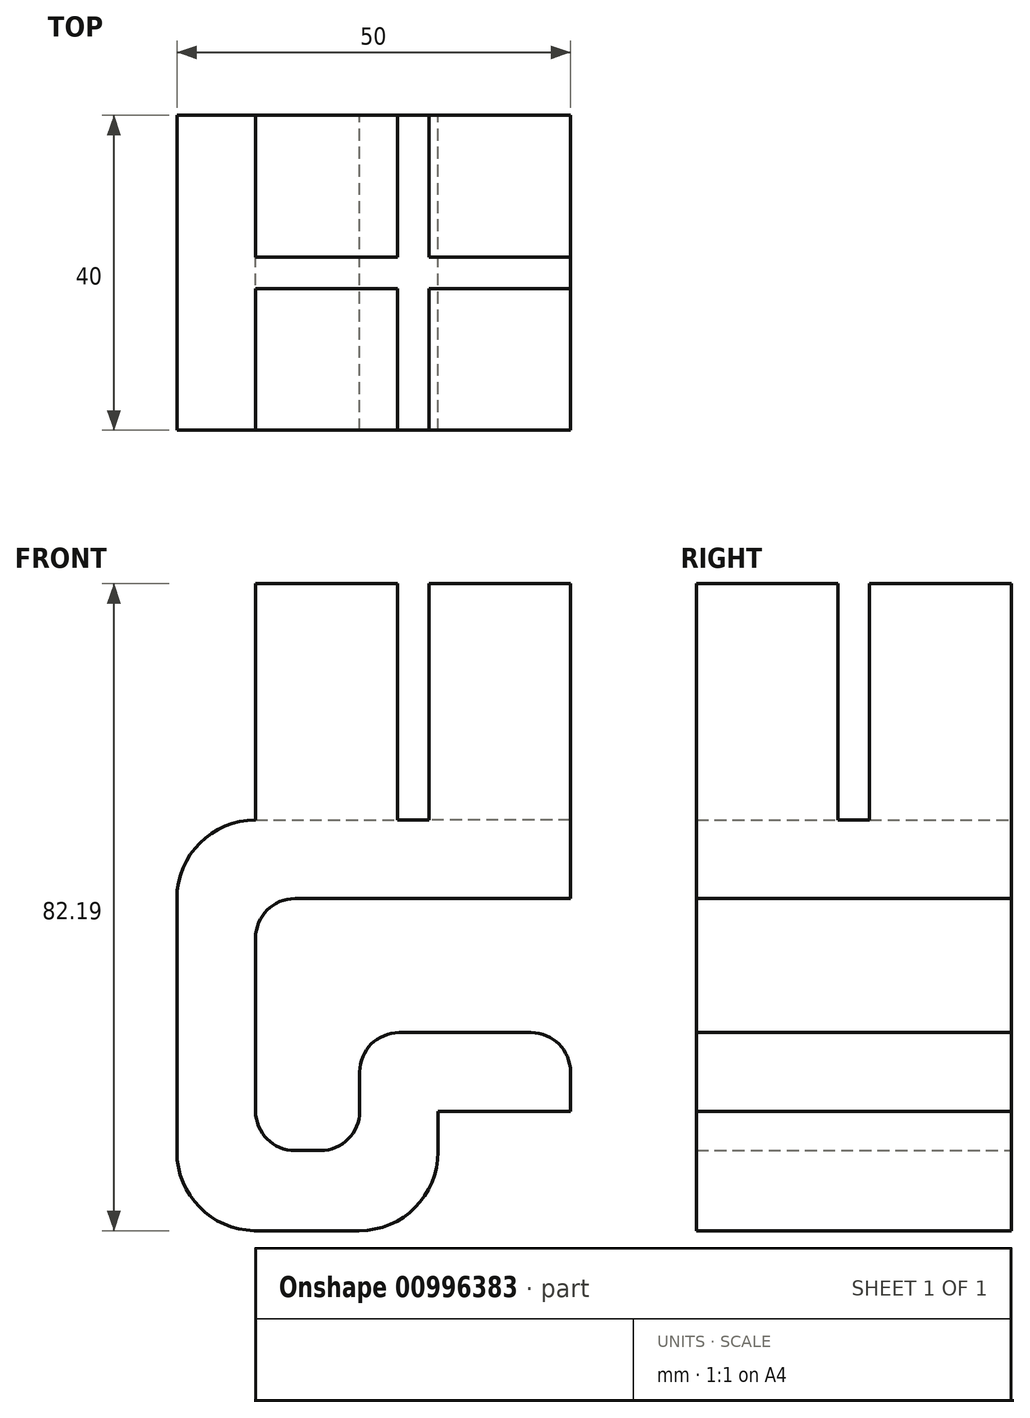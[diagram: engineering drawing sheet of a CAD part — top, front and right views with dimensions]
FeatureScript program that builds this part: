
annotation { "Feature Type Name" : "Feature", "Feature Type Description" : "" }
export const myFeature = defineFeature(function(context is Context, id is Id, definition is map)
    precondition{}
    {
        {
            var Q0;
            Q0=qCreatedBy(makeId("Front.planeOp"),FACE);
            var sketch = newSketch(context, id + "F0", { "sketchPlane" : qUnion([Q0])});
            skLineSegment(sketch, "E0.bottom", {"start": v(20, -5) * mm, "end": v(-10, -5) * mm});
            skLineSegment(sketch, "E0.top", {"start": v(20, 5) * mm, "end": v(-20, 5) * mm});
            skLineSegment(sketch, "E0.left", {"start": v(20, -5) * mm, "end": v(20, 5) * mm});
            skPoint(sketch, "E0.middle", {"position": v(0, 0) * mm});
            skLineSegment(sketch, "E1.top", {"start": v(-20, 5) * mm, "end": v(-20, 5) * mm});
            skLineSegment(sketch, "E1.right", {"start": v(-30, -5) * mm, "end": v(-30, -5) * mm});
            skPoint(sketch, "E1.middle", {"position": v(-25, 0) * mm});
            skPoint(sketch, "E2.visualSharp", {"position": v(-30, 5) * mm});
            skArc(sketch, "E2.filletArc", {"start": v(-20, 5) * mm, "mid": v(-27.07, 2.07) * mm, "end": v(-30, -5) * mm});
            skLineSegment(sketch, "E3", {"start": v(0, -5) * mm, "end": v(0, -22) * mm, "construction": true});
            skLineSegment(sketch, "E4", {"start": v(-30, -5) * mm, "end": v(-30, -37) * mm});
            skLineSegment(sketch, "E5", {"start": v(-20, -15) * mm, "end": v(-20, -32) * mm});
            skLineSegment(sketch, "E6", {"start": v(-10, -5) * mm, "end": v(-15, -5) * mm});
            skLineSegment(sketch, "E7", {"start": v(-20, -15) * mm, "end": v(-20, -10) * mm});
            skArc(sketch, "E8.filletArc", {"start": v(-15, -5) * mm, "mid": v(-18.54, -6.46) * mm, "end": v(-20, -10) * mm});
            skLineSegment(sketch, "E9.bottom", {"start": v(-48.31, -24.83) * mm, "end": v(-58.31, -24.83) * mm});
            skLineSegment(sketch, "E9.top", {"start": v(-48.31, -14.83) * mm, "end": v(-58.31, -14.83) * mm});
            skLineSegment(sketch, "E9.left", {"start": v(-48.31, -24.83) * mm, "end": v(-48.31, -14.83) * mm});
            skLineSegment(sketch, "E9.right", {"start": v(-58.31, -24.83) * mm, "end": v(-58.31, -14.83) * mm});
            skPoint(sketch, "E9.middle", {"position": v(-53.31, -19.83) * mm});
            skLineSegment(sketch, "E10.bottom", {"start": v(-20, -47.2) * mm, "end": v(-20.18, -47.19) * mm});
            skLineSegment(sketch, "E10.right", {"start": v(-30, -37.2) * mm, "end": v(-30, -37) * mm});
            skPoint(sketch, "E10.middle", {"position": v(-25, -42.1) * mm});
            skLineSegment(sketch, "E11.bottom", {"start": v(-10, -47.2) * mm, "end": v(-20, -47.2) * mm});
            skPoint(sketch, "E12.visualSharp", {"position": v(-30, -47) * mm});
            skArc(sketch, "E12.filletArc", {"start": v(-30, -37.2) * mm, "mid": v(-27.13, -44.2) * mm, "end": v(-20.18, -47.19) * mm});
            skPoint(sketch, "E13.visualSharp", {"position": v(-20, -37) * mm});
            skArc(sketch, "E13.filletArc", {"start": v(-20, -32) * mm, "mid": v(-18.54, -35.54) * mm, "end": v(-15, -37) * mm});
            skLineSegment(sketch, "E14.bottom", {"start": v(-6.83, -47.2) * mm, "end": v(-10, -47.2) * mm});
            skLineSegment(sketch, "E15.bottom", {"start": v(-6.83, -47.2) * mm, "end": v(-6.83, -47.2) * mm});
            skPoint(sketch, "E15.middle", {"position": v(-1.83, -42.1) * mm});
            skPoint(sketch, "E16.middle", {"position": v(-4.81, -36.07) * mm});
            skPoint(sketch, "E17.visualSharp", {"position": v(3.17, -47.2) * mm});
            skArc(sketch, "E17.filletArc", {"start": v(-6.83, -47.2) * mm, "mid": v(0.24, -44.26) * mm, "end": v(3.17, -37.2) * mm});
            skPoint(sketch, "E18.visualSharp", {"position": v(-6.83, -37) * mm});
            skArc(sketch, "E18.filletArc", {"start": v(-11.77, -37) * mm, "mid": v(-8.24, -35.55) * mm, "end": v(-6.77, -32.03) * mm});
            skLineSegment(sketch, "E19.top", {"start": v(3.17, -22.03) * mm, "end": v(-1.77, -22.03) * mm});
            skLineSegment(sketch, "E19.right", {"start": v(-6.77, -32.03) * mm, "end": v(-6.77, -27.03) * mm});
            skPoint(sketch, "E19.middle", {"position": v(-1.8, -27.03) * mm});
            skPoint(sketch, "E20.visualSharp", {"position": v(-6.77, -22.03) * mm});
            skArc(sketch, "E20.filletArc", {"start": v(-1.77, -22.03) * mm, "mid": v(-5.3, -23.5) * mm, "end": v(-6.77, -27.03) * mm});
            skLineSegment(sketch, "E21", {"start": v(3.17, -22.03) * mm, "end": v(15, -22.03) * mm});
            skPoint(sketch, "E22.visualSharp", {"position": v(-2.8, -35.13) * mm});
            skLineSegment(sketch, "E23", {"start": v(3.17, -37.2) * mm, "end": v(3.17, -32.03) * mm});
            skLineSegment(sketch, "E24", {"start": v(20, -27.03) * mm, "end": v(20, -32.03) * mm});
            skLineSegment(sketch, "E25", {"start": v(20, -32.03) * mm, "end": v(3.17, -32.03) * mm});
            skPoint(sketch, "E26.visualSharp", {"position": v(20, -22.03) * mm});
            skArc(sketch, "E26.filletArc", {"start": v(20, -27.03) * mm, "mid": v(18.54, -23.5) * mm, "end": v(15, -22.03) * mm});
            skLineSegment(sketch, "E27", {"start": v(-11.77, -37) * mm, "end": v(-15, -37) * mm});
            skLineSegment(sketch, "E28", {"start": v(20, -5) * mm, "end": v(20, -41.06) * mm, "construction": true});
            skSolve(sketch);
        }
        {
            var Q0;
            Q0=makeQuery(id+"F0.imprint","IMPRINT",FACE,{"disambiguationData":[TD([[makeQuery(id+"F0.imprint","IMPRINT",EDGE,{"derivedFrom":sQuery(id+"F0.wireOp",EDGE,"E0.bottom")}),-1.0]])]});
            var Q1;
            Q1=makeQuery(id+"F0.imprint","IMPRINT",FACE,{"disambiguationData":[TD([[makeQuery(id+"F0.imprint","IMPRINT",EDGE,{"derivedFrom":sQuery(id+"F0.wireOp",EDGE,"E15.right")}),-1.0]])]});
            var Q2;
            Q2=makeQuery(id+"F0.imprint","IMPRINT",FACE,{"disambiguationData":[TD([[makeQuery(id+"F0.imprint","IMPRINT",EDGE,{"derivedFrom":sQuery(id+"F0.wireOp",EDGE,"E19.bottom")}),-1.0]])]});
            var Q3;
            Q3=makeQuery(id+"F0.imprint","IMPRINT",FACE,{"disambiguationData":[TD([[makeQuery(id+"F0.imprint","IMPRINT",EDGE,{"derivedFrom":sQuery(id+"F0.wireOp",EDGE,"E14.bottom")}),-1.0]])]});
            extrude(context, id + "F1", {"entities" : qUnion([Q0, Q1, Q2, Q3]), "endBound" : BoundingType.SYMMETRIC, "depth" : 40 * mm, "offsetDistance" : 25 * mm});
        }
        {
            var Q0;
            Q0=makeQuery(id+"F1.opExtrude","SWEPT_FACE",FACE,{"disambiguationData":[OSD([sQuery(id+"F0.wireOp",EDGE,"E0.top")])]});
            var sketch = newSketch(context, id + "F2", { "sketchPlane" : qUnion([Q0])});
            skLineSegment(sketch, "E29.left", {"start": v(0, -20) * mm, "end": v(0, 20) * mm});
            skLineSegment(sketch, "E30.bottom", {"start": v(42.29, 17.77) * mm, "end": v(44.29, 17.77) * mm});
            skLineSegment(sketch, "E30.top", {"start": v(42.29, 57.77) * mm, "end": v(44.29, 57.77) * mm});
            skPoint(sketch, "E30.middle", {"position": v(43.29, 37.77) * mm});
            skLineSegment(sketch, "E31", {"start": v(0, 20) * mm, "end": v(-10, 20) * mm});
            skLineSegment(sketch, "E32", {"start": v(-10, 20) * mm, "end": v(-10, -20) * mm});
            skLineSegment(sketch, "E33", {"start": v(-10, -20) * mm, "end": v(0, -20) * mm});
            skLineSegment(sketch, "E34", {"start": v(0, 20) * mm, "end": v(10, 20) * mm});
            skLineSegment(sketch, "E35", {"start": v(10, 20) * mm, "end": v(10, -20) * mm});
            skLineSegment(sketch, "E36", {"start": v(10, -20) * mm, "end": v(0, -20) * mm});
            skSolve(sketch);
        }
        {
            var Q0;
            {var subQ0=sQuery(id+"F2.wireOp",EDGE,"E29.left");Q0=makeQuery(id+"F2.imprint","IMPRINT",FACE,{"disambiguationData":[TD([[makeQuery(id+"F2.imprint","IMPRINT",EDGE,{"derivedFrom":subQ0}),-1.0]])]});}
            var Q1;
            {var subQ4=sQuery(id+"F2.wireOp",EDGE,"E29.bottom");Q1=makeQuery(id+"F2.imprint","IMPRINT",FACE,{"disambiguationData":[TD([[makeQuery(id+"F2.imprint","IMPRINT",EDGE,{"derivedFrom":subQ4}),-1.0]])]});}
            var Q2;
            Q2=makeQuery(id+"F2.imprint","IMPRINT",FACE,{"disambiguationData":[TD([[makeQuery(id+"F2.imprint","IMPRINT",EDGE,{"derivedFrom":sQuery(id+"F2.wireOp",EDGE,"E29.left")}),1.0]])]});
            var Q3;
            {var subQ0=sQuery(id+"F2.wireOp",EDGE,"E32");Q3=makeQuery(id+"F2.imprint","IMPRINT",FACE,{"disambiguationData":[TD([[makeQuery(id+"F2.imprint","IMPRINT",EDGE,{"derivedFrom":subQ0}),-1.0]])]});}
            var Q4;
            {var subQ0=sQuery(id+"F2.wireOp",EDGE,"E35");Q4=makeQuery(id+"F2.imprint","IMPRINT",FACE,{"disambiguationData":[TD([[makeQuery(id+"F2.imprint","IMPRINT",EDGE,{"derivedFrom":subQ0}),1.0]])]});}
            extrude(context, id + "F3", {"entities" : qUnion([Q0, Q1, Q2, Q3, Q4]), "operationType" : NewBodyOperationType.ADD, "depth" : 30 * mm, "offsetDistance" : 25 * mm});
        }
        {
            var Q0;
            Q0=makeQuery(id+"F3.opExtrude","CAP_FACE",FACE,{"disambiguationData":[OSD([sQuery(id+"F2.wireOp",EDGE,"E31"),sQuery(id+"F2.wireOp",EDGE,"E32"),sQuery(id+"F2.wireOp",EDGE,"E33"),sQuery(id+"F2.wireOp",EDGE,"E34"),sQuery(id+"F2.wireOp",EDGE,"E35"),sQuery(id+"F2.wireOp",EDGE,"E36")])],"isStart":false});
            var sketch = newSketch(context, id + "F4", { "sketchPlane" : qUnion([Q0])});
            skLineSegment(sketch, "E37", {"start": v(0, 20) * mm, "end": v(0, -20) * mm});
            skLineSegment(sketch, "E38", {"start": v(0, -20) * mm, "end": v(2, -20) * mm});
            skLineSegment(sketch, "E39", {"start": v(2, -20) * mm, "end": v(2, 20) * mm});
            skLineSegment(sketch, "E40", {"start": v(2, 20) * mm, "end": v(0, 20) * mm});
            skLineSegment(sketch, "E41", {"start": v(0, 20) * mm, "end": v(-2, 20) * mm});
            skLineSegment(sketch, "E42", {"start": v(-2, 20) * mm, "end": v(-2, -20) * mm});
            skLineSegment(sketch, "E43", {"start": v(-2, -20) * mm, "end": v(0, -20) * mm});
            skLineSegment(sketch, "E44", {"start": v(-20, 0) * mm, "end": v(20, 0) * mm});
            skLineSegment(sketch, "E45", {"start": v(20, 0) * mm, "end": v(20, -2) * mm});
            skLineSegment(sketch, "E46", {"start": v(20, -2) * mm, "end": v(-20, -2) * mm});
            skLineSegment(sketch, "E47", {"start": v(-20, -2) * mm, "end": v(-20, 0) * mm});
            skLineSegment(sketch, "E48", {"start": v(-20, 0) * mm, "end": v(-20, 2) * mm});
            skLineSegment(sketch, "E49", {"start": v(-20, 2) * mm, "end": v(20, 2) * mm});
            skLineSegment(sketch, "E50", {"start": v(20, 2) * mm, "end": v(20, 0) * mm});
            skSolve(sketch);
        }
        {
            var Q0;
            Q0=makeQuery(id+"F4.imprint","IMPRINT",FACE,{"disambiguationData":[TD([[makeQuery(id+"F4.imprint","IMPRINT",EDGE,{"derivedFrom":sQuery(id+"F4.wireOp",EDGE,"E37")}),-1.0]])]});
            var Q1;
            Q1=makeQuery(id+"F4.imprint","IMPRINT",FACE,{"disambiguationData":[TD([[makeQuery(id+"F4.imprint","IMPRINT",EDGE,{"derivedFrom":sQuery(id+"F4.wireOp",EDGE,"E37")}),1.0]])]});
            var Q2;
            {var subQ5=sQuery(id+"F4.wireOp",EDGE,"E50");Q2=makeQuery(id+"F4.imprint","IMPRINT",FACE,{"disambiguationData":[TD([[makeQuery(id+"F4.imprint","IMPRINT",EDGE,{"derivedFrom":subQ5}),1.0]])]});}
            var Q3;
            {var subQ5=sQuery(id+"F4.wireOp",EDGE,"E45");Q3=makeQuery(id+"F4.imprint","IMPRINT",FACE,{"disambiguationData":[TD([[makeQuery(id+"F4.imprint","IMPRINT",EDGE,{"derivedFrom":subQ5}),1.0]])]});}
            var Q4;
            {var subQ5=sQuery(id+"F4.wireOp",EDGE,"E47");Q4=makeQuery(id+"F4.imprint","IMPRINT",FACE,{"disambiguationData":[TD([[makeQuery(id+"F4.imprint","IMPRINT",EDGE,{"derivedFrom":subQ5}),-1.0]])]});}
            var Q5;
            {var subQ5=sQuery(id+"F4.wireOp",EDGE,"E48");Q5=makeQuery(id+"F4.imprint","IMPRINT",FACE,{"disambiguationData":[TD([[makeQuery(id+"F4.imprint","IMPRINT",EDGE,{"derivedFrom":subQ5}),-1.0]])]});}
            extrude(context, id + "F5", {"entities" : qUnion([Q0, Q1, Q2, Q3, Q4, Q5]), "operationType" : NewBodyOperationType.REMOVE, "oppositeDirection" : true, "depth" : 30 * mm, "offsetDistance" : 25 * mm});
        }
    });
